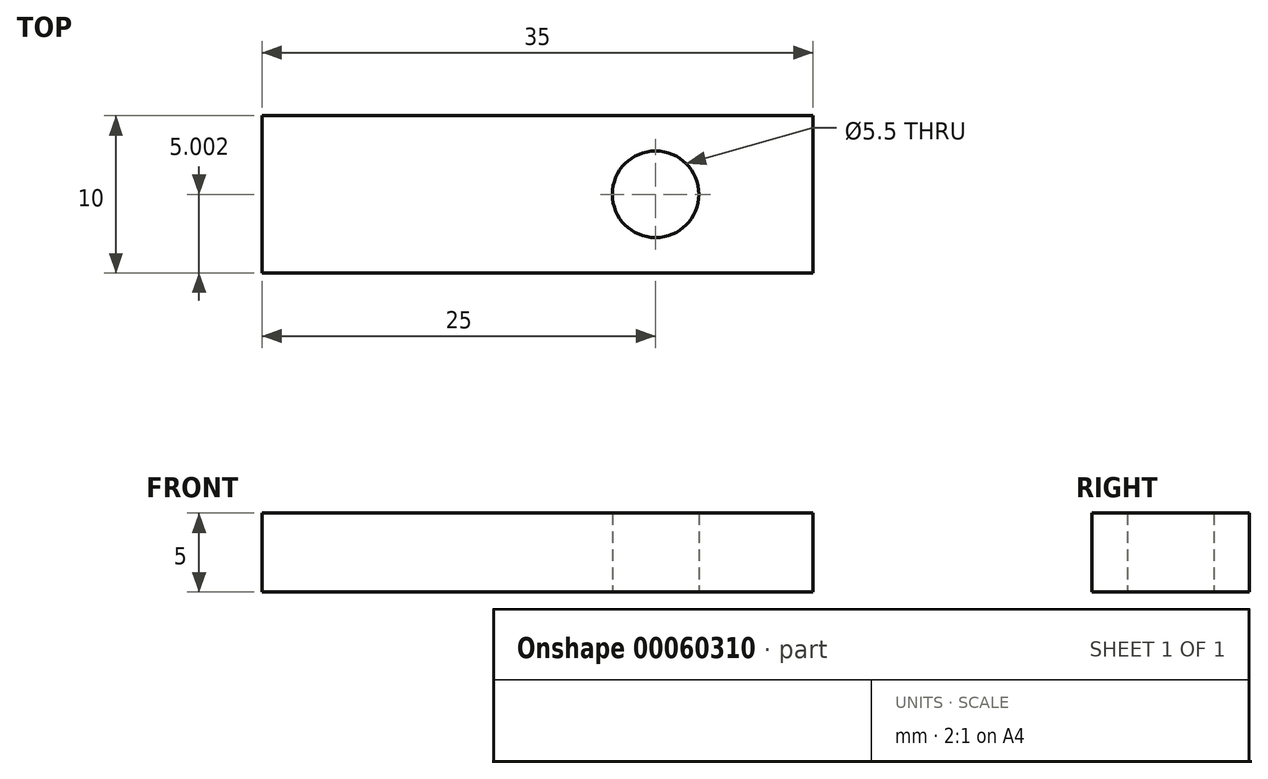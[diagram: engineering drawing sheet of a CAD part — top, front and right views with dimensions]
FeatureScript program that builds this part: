
annotation { "Feature Type Name" : "Feature", "Feature Type Description" : "" }
export const myFeature = defineFeature(function(context is Context, id is Id, definition is map)
    precondition{}
    {
        {
            var Q0;
            Q0=qCreatedBy(makeId("Top.planeOp"),FACE);
            var sketch = newSketch(context, id + "F0", { "sketchPlane" : qUnion([Q0])});
            skLineSegment(sketch, "E0.bottom", {"start": v(-14.02, 3.78) * mm, "end": v(20.98, 3.78) * mm});
            skLineSegment(sketch, "E0.top", {"start": v(-14.02, -6.22) * mm, "end": v(20.98, -6.22) * mm});
            skLineSegment(sketch, "E0.left", {"start": v(-14.02, 3.78) * mm, "end": v(-14.02, -6.22) * mm});
            skLineSegment(sketch, "E0.right", {"start": v(20.98, 3.78) * mm, "end": v(20.98, -6.22) * mm});
            skLineSegment(sketch, "E1", {"start": v(10.98, 3.78) * mm, "end": v(10.98, -6.22) * mm, "construction": true});
            skCircle(sketch, "E2", {"center": v(10.98, -1.22) * mm, "radius": 2.75 * mm});
            skSolve(sketch);
        }
        {
            var Q0;
            Q0=qSketchRegion(id+"F0",true);
            extrude(context, id + "F1", {"entities" : qUnion([Q0]), "depth" : 5 * mm});
        }
    });
